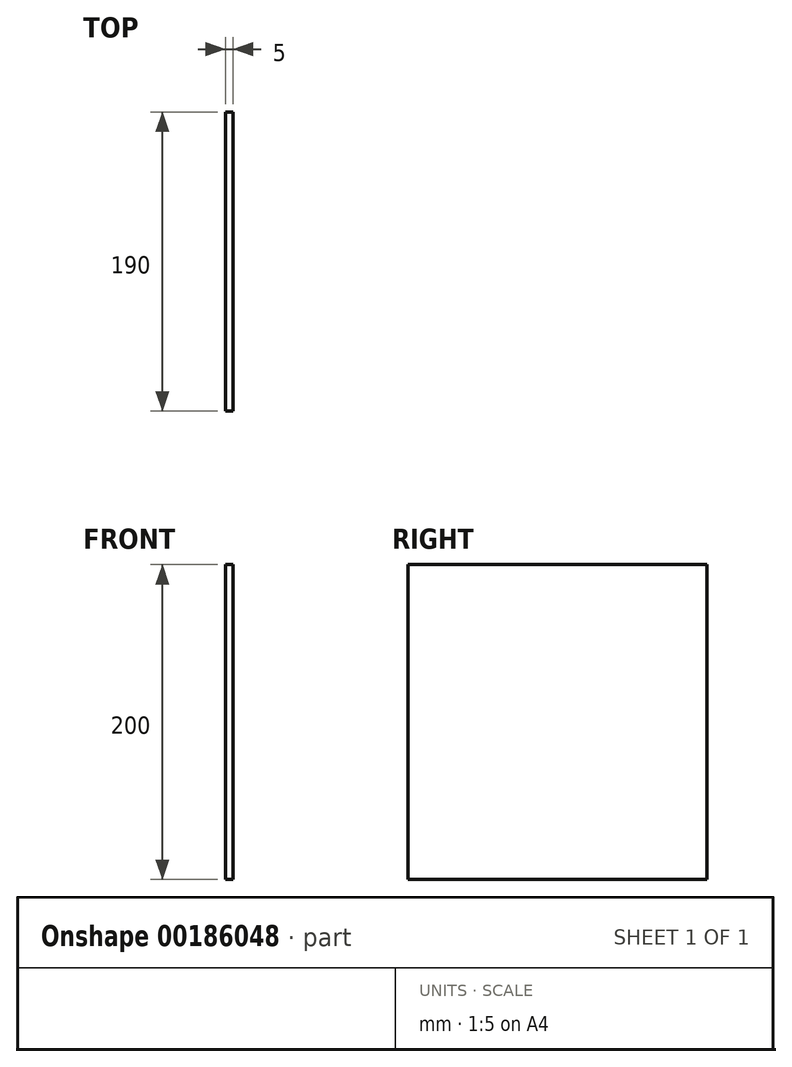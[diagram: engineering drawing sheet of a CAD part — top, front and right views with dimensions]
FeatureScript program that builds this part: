
annotation { "Feature Type Name" : "Feature", "Feature Type Description" : "" }
export const myFeature = defineFeature(function(context is Context, id is Id, definition is map)
    precondition{}
    {
        {
            var Q0;
            Q0=qCreatedBy(makeId("Right.planeOp"),FACE);
            var sketch = newSketch(context, id + "F0", { "sketchPlane" : qUnion([Q0])});
            skLineSegment(sketch, "E0.bottom", {"start": v(-95, 0) * mm, "end": v(95, 0) * mm});
            skLineSegment(sketch, "E0.top", {"start": v(-95, 200) * mm, "end": v(95, 200) * mm});
            skLineSegment(sketch, "E0.left", {"start": v(-95, 0) * mm, "end": v(-95, 200) * mm});
            skLineSegment(sketch, "E0.right", {"start": v(95, 0) * mm, "end": v(95, 200) * mm});
            skSolve(sketch);
        }
        {
            var Q0;
            Q0 = qSketchRegion(id + "F0", true);
            extrude(context, id + "F1", {"entities" : qUnion([Q0]), "endBound" : BoundingType.SYMMETRIC, "depth" : 5 * mm});
        }
    });
